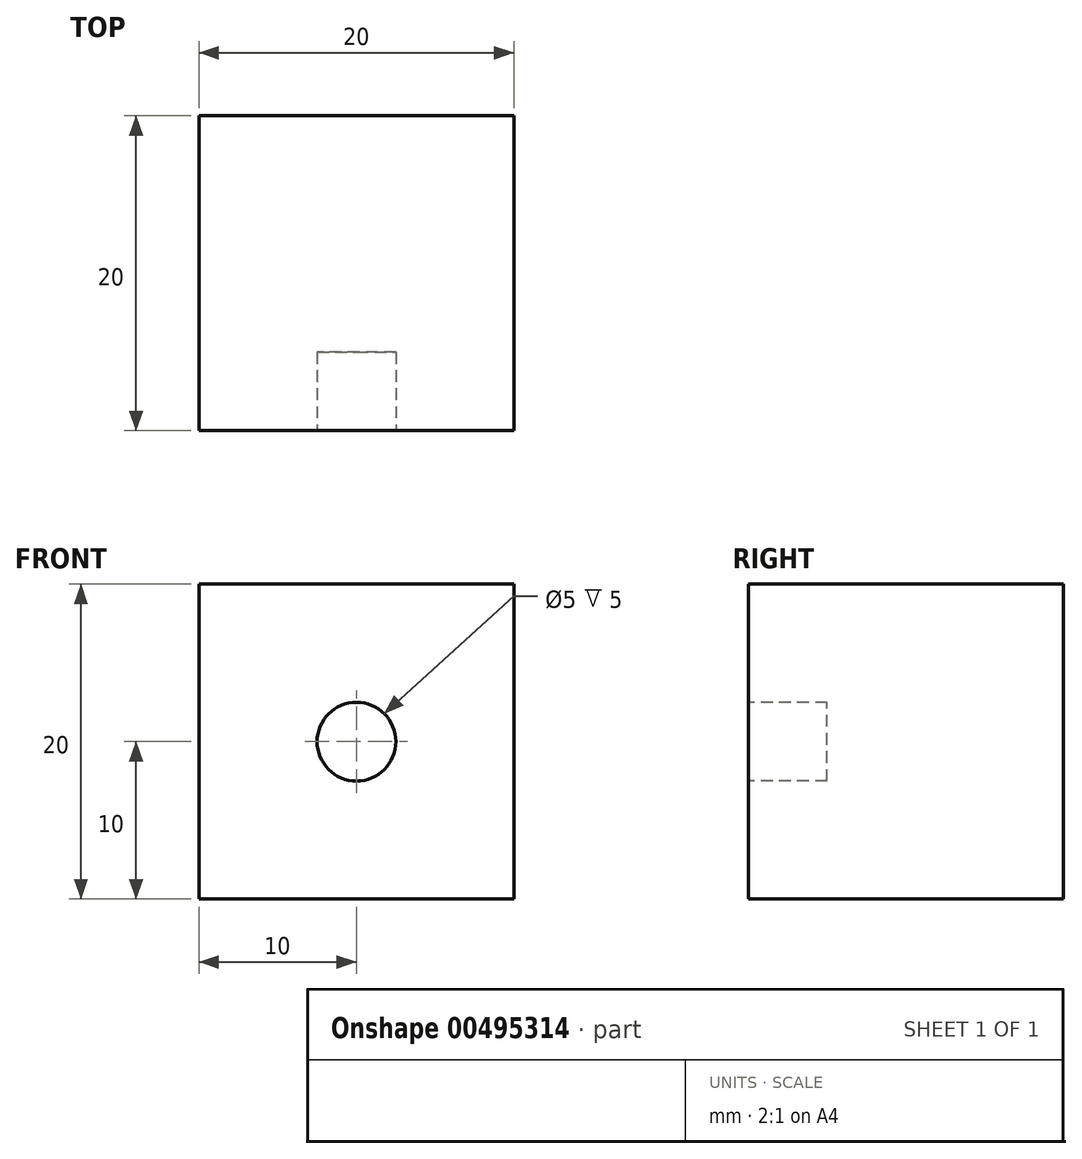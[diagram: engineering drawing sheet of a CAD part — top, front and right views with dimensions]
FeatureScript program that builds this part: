
annotation { "Feature Type Name" : "Feature", "Feature Type Description" : "" }
export const myFeature = defineFeature(function(context is Context, id is Id, definition is map)
    precondition{}
    {
        {
            var Q0;
            Q0=qCreatedBy(makeId("Top.planeOp"),FACE);
            var sketch = newSketch(context, id + "F0", { "sketchPlane" : qUnion([Q0])});
            skLineSegment(sketch, "E0.bottom", {"start": v(10, -10) * mm, "end": v(-10, -10) * mm});
            skLineSegment(sketch, "E0.top", {"start": v(10, 10) * mm, "end": v(-10, 10) * mm});
            skLineSegment(sketch, "E0.left", {"start": v(10, -10) * mm, "end": v(10, 10) * mm});
            skLineSegment(sketch, "E0.right", {"start": v(-10, -10) * mm, "end": v(-10, 10) * mm});
            skPoint(sketch, "E0.middle", {"position": v(0, 0) * mm});
            skSolve(sketch);
        }
        {
            var Q0;
            Q0 = qSketchRegion(id + "F0", true);
            extrude(context, id + "F1", {"entities" : qUnion([Q0]), "depth" : 20 * mm});
        }
        {
            var Q0;
            Q0=makeQuery(id+"F1.opExtrude","SWEPT_FACE",FACE,{"disambiguationData":[OSD([sQuery(id+"F0.wireOp",EDGE,"E0.bottom")])]});
            var sketch = newSketch(context, id + "F2", { "sketchPlane" : qUnion([Q0])});
            skCircle(sketch, "E1", {"center": v(0, 10) * mm, "radius": 2.5 * mm});
            skSolve(sketch);
        }
        {
            var Q0;
            Q0=makeQuery(id+"F2.imprint","IMPRINT",FACE,{"disambiguationData":[TD([[makeQuery(id+"F2.imprint","IMPRINT",EDGE,{"derivedFrom":sQuery(id+"F2.wireOp",EDGE,"E1")}),1.0]])]});
            extrude(context, id + "F3", {"entities" : qUnion([Q0]), "operationType" : NewBodyOperationType.REMOVE, "oppositeDirection" : true, "depth" : 5 * mm});
        }
    });
